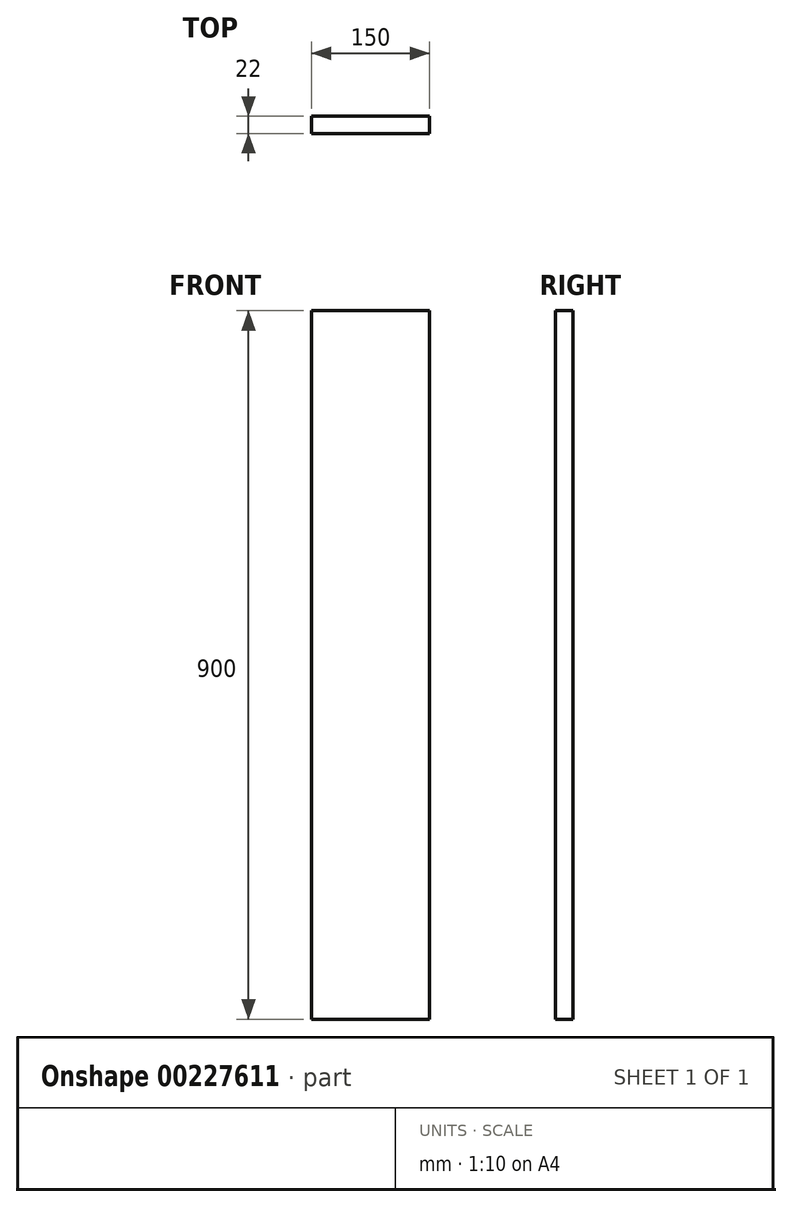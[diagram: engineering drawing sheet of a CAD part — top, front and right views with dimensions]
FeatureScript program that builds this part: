
annotation { "Feature Type Name" : "Feature", "Feature Type Description" : "" }
export const myFeature = defineFeature(function(context is Context, id is Id, definition is map)
    precondition{}
    {
        {
            var Q0;
            Q0=qCreatedBy(makeId("Front.planeOp"),FACE);
            var sketch = newSketch(context, id + "F0", { "sketchPlane" : qUnion([Q0])});
            skLineSegment(sketch, "E0.bottom", {"start": v(75, 450) * mm, "end": v(-75, 450) * mm});
            skLineSegment(sketch, "E0.top", {"start": v(75, -450) * mm, "end": v(-75, -450) * mm});
            skLineSegment(sketch, "E0.left", {"start": v(75, 450) * mm, "end": v(75, -450) * mm});
            skLineSegment(sketch, "E0.right", {"start": v(-75, 450) * mm, "end": v(-75, -450) * mm});
            skPoint(sketch, "E0.middle", {"position": v(0, 0) * mm});
            skSolve(sketch);
        }
        {
            var Q0;
            Q0=qSketchRegion(id+"F0",true);
            extrude(context, id + "F1", {"entities" : qUnion([Q0]), "depth" : 22 * mm});
        }
    });
